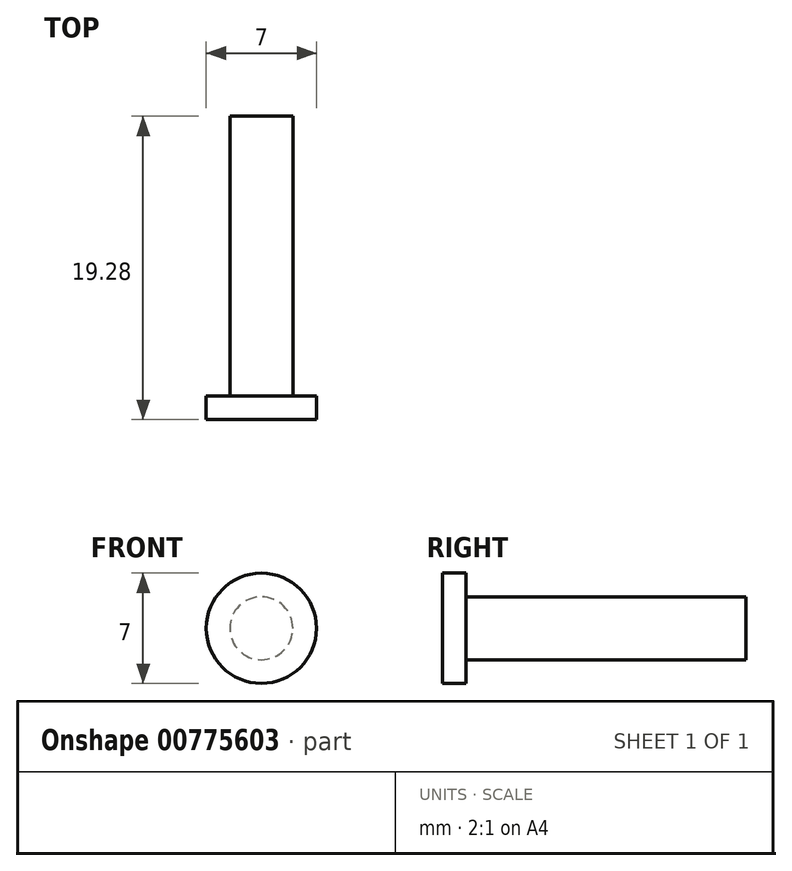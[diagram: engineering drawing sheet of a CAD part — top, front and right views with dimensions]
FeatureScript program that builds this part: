
annotation { "Feature Type Name" : "Feature", "Feature Type Description" : "" }
export const myFeature = defineFeature(function(context is Context, id is Id, definition is map)
    precondition{}
    {
        {
            var Q0;
            Q0=qCreatedBy(makeId("Front.planeOp"),FACE);
            var sketch = newSketch(context, id + "F0", { "sketchPlane" : qUnion([Q0])});
            skCircle(sketch, "E0", {"center": v(0, 0) * mm, "radius": 2 * mm});
            skSolve(sketch);
        }
        {
            var Q0;
            Q0 = qSketchRegion(id + "F0", true);
            extrude(context, id + "F1", {"entities" : qUnion([Q0]), "depth" : 12.7 * mm + 5.08 * mm, "offsetDistance" : 25.4 * mm});
        }
        {
            var Q0;
            Q0=makeQuery(id+"F1.opExtrude","CAP_FACE",FACE,{"disambiguationData":[OSD([sQuery(id+"F0.wireOp",EDGE,"E0")])],"isStart":false});
            var sketch = newSketch(context, id + "F2", { "sketchPlane" : qUnion([Q0])});
            skCircle(sketch, "E1", {"center": v(0, 0) * mm, "radius": 3.5 * mm});
            skSolve(sketch);
        }
        {
            var Q0;
            Q0 = qSketchRegion(id + "F2", true);
            extrude(context, id + "F3", {"entities" : qUnion([Q0]), "operationType" : NewBodyOperationType.ADD, "depth" : 1.5 * mm, "offsetDistance" : 25.4 * mm});
        }
    });
